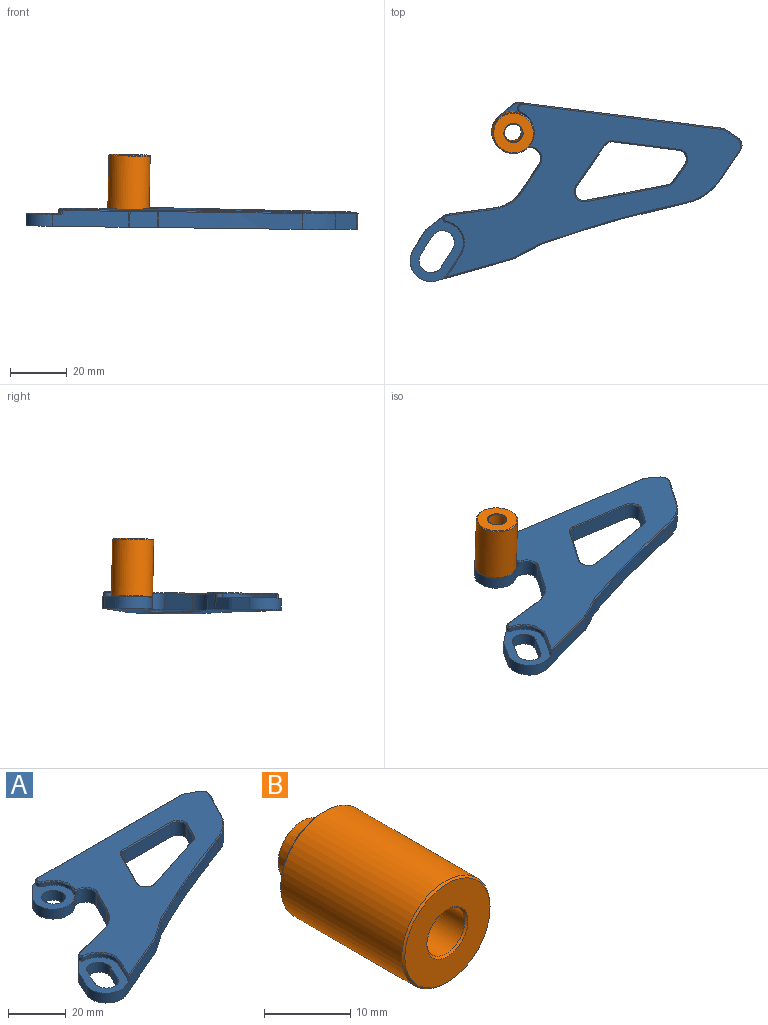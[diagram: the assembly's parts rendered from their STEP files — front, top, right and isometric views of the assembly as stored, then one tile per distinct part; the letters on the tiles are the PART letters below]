
ASSEMBLY  parts=2 mates=1
PART A: 80 faces, bbox 110.9x66.7x6.3 mm
  f0: plane 17.76x14.5mm, normal (0,0,1), area 122.4mm2, adj f1,f2,f3,f13,f14,f15,f16,f17
  f1: cylinder r=1.82mm len=3.56mm, axis (0,0,-1), area 7.5mm2, adj f0,f2,f13,f60
  f2: cylinder r=7.24mm len=10.45mm, axis (0,0,-1), area 18.8mm2, adj f0,f1,f3,f61
  f3: cylinder r=0.76mm len=1.45mm, axis (0,0,-1), area 2.3mm2, adj f0,f2,f17,f62
  f4: cylinder r=7.33mm len=1.72mm, axis (0,0,-1), area 3mm2, adj f5,f69,f70,f71
  f5: plane 6.75x3.15mm, normal (-0.91,0.42,0), area 10.8mm2, adj f4,f6,f50,f71
  f6: cylinder r=7.33mm len=10.42mm, axis (0,0,-1), area 21mm2, adj f5,f7,f49,f71
  f7: cylinder r=1.2mm len=2.05mm, axis (0,0,-1), area 4mm2, adj f6,f21,f68,f71
  f8: cylinder r=19.05mm len=10.67mm, axis (0,0,1), area 81.1mm2, adj f9,f26,f54,f73
  f9: plane 11.36x5.79mm, normal (0.89,-0.45,0), area 71.3mm2, adj f8,f10,f55,f73
  f10: cylinder r=3.17mm len=5.59mm, axis (0,0,1), area 27.9mm2, adj f9,f11,f56,f73
  f11: plane 5.59x4.46mm, normal (0.45,0.89,0), area 28mm2, adj f10,f12,f57,f73
  f12: cylinder r=3.17mm len=5.59mm, axis (0,0,1), area 8.4mm2, adj f11,f13,f58,f73
  f13: plane 71.53x5.59mm, normal (0,1,0), area 398mm2, adj f0,f1,f12,f14,f59,f73
  f14: cylinder r=3.17mm len=4.14mm, axis (0,0,1), area 10.7mm2, adj f0,f13,f15,f73
  f15: plane 4.54x4.31mm, normal (-0.72,0.69,0), area 25.9mm2, adj f0,f14,f16,f73
  f16: cylinder r=7.24mm len=12.23mm, axis (0,0,-1), area 90.8mm2, adj f0,f15,f17,f73
  f17: cylinder r=3.92mm len=6.45mm, axis (0,0,1), area 56.4mm2, adj f0,f3,f16,f18,f63,f73
  f18: plane 10.44x5.59mm, normal (-0.89,0.46,0), area 65.5mm2, adj f17,f19,f64,f73
  f19: cylinder r=12.7mm len=8.04mm, axis (0,0,1), area 59.4mm2, adj f18,f20,f65,f73
  f20: plane 15.92x5.59mm, normal (-0.26,0.97,0), area 92mm2, adj f19,f21,f66,f73
  f21: cylinder r=3.17mm len=5.59mm, axis (0,0,1), area 9.3mm2, adj f7,f20,f22,f67,f73
  f22: plane 5.41x5.41mm, normal (-0.71,0.71,0), area 31.7mm2, adj f21,f23,f71,f73
  f23: cylinder r=3.17mm len=4.14mm, axis (0,0,1), area 4.6mm2, adj f22,f24,f71,f73
  f24: plane 6.71x4.14mm, normal (-0.91,0.42,0), area 30.7mm2, adj f23,f71,f72,f73
  f25: cylinder r=3.17mm len=5.59mm, axis (0,0,1), area 2.5mm2, adj f26,f40,f52,f73
  f26: cylinder r=406.4mm len=48.32mm, axis (0,0,-1), area 293.6mm2, adj f8,f25,f53,f73
  f27: cylinder r=3.17mm len=5.59mm, axis (0,0,-1), area 19.5mm2, adj f28,f34,f48,f73
  f28: plane 23.14x5.59mm, normal (0,-1,0), area 129.3mm2, adj f27,f29,f41,f73
  f29: cylinder r=3.17mm len=5.59mm, axis (0,0,-1), area 36.2mm2, adj f28,f30,f42,f73
  f30: plane 6.39x5.59mm, normal (-0.89,0.45,0), area 40.1mm2, adj f29,f31,f43,f73
  f31: cylinder r=3.17mm len=5.59mm, axis (0,0,-1), area 13.9mm2, adj f30,f32,f44,f73
  f32: plane 27.77x9.02mm, normal (-0.31,0.95,0), area 163.2mm2, adj f31,f33,f45,f73
  f33: cylinder r=3.17mm len=5.59mm, axis (0,0,-1), area 41.8mm2, adj f32,f34,f46,f73
  f34: plane 15.41x7.89mm, normal (0.89,-0.46,0), area 96.8mm2, adj f27,f33,f47,f73
  f35: cylinder r=4.09mm len=8.18mm, axis (0,0,1), area 106.4mm2, adj f0,f73
  f36: plane 6.75x4.14mm, normal (-0.91,0.42,0), area 30.8mm2, adj f37,f39,f71,f73
  f37: cylinder r=4.23mm len=8.06mm, axis (0,0,1), area 55mm2, adj f36,f38,f71,f73
  f38: plane 6.75x4.14mm, normal (0.91,-0.42,0), area 30.8mm2, adj f37,f39,f71,f73
  f39: cylinder r=4.23mm len=8.06mm, axis (0,0,1), area 55mm2, adj f36,f38,f71,f73
  f40: plane 8.85x6.16mm, normal (0.57,-0.82,0), area 60.2mm2, adj f25,f51,f73,f74
  f41: plane 23.14x0.38mm, normal (0,-0.71,0.71), area 12.5mm2, adj f28,f42,f48,f76
  f42: cone r=3.37mm half-angle=45deg, axis (0,0,1), area 3.7mm2, adj f29,f41,f43,f76
  f43: plane 6.56x3.59mm, normal (-0.63,0.32,0.71), area 3.9mm2, adj f30,f42,f44,f76
  f44: cone r=3.37mm half-angle=45deg, axis (0,0,1), area 1.4mm2, adj f31,f43,f45,f76
  f45: plane 27.89x9.39mm, normal (-0.22,0.67,0.71), area 15.7mm2, adj f32,f44,f46,f76
  f46: cone r=3.37mm half-angle=45deg, axis (0,0,1), area 4.3mm2, adj f33,f45,f47,f76
  f47: plane 15.59x8.23mm, normal (0.63,-0.32,0.71), area 9.3mm2, adj f34,f46,f48,f76
  f48: cone r=3.37mm half-angle=45deg, axis (0,0,1), area 2mm2, adj f27,f41,f47,f76
  f49: cone r=7.52mm half-angle=45deg, axis (0,0,1), area 8mm2, adj f6,f50,f68,f76
  f50: plane 6.91x3.49mm, normal (-0.64,0.3,0.71), area 4mm2, adj f5,f49,f69,f76
  f51: plane 9.07x6.47mm, normal (0.4,-0.58,0.71), area 5.8mm2, adj f40,f52,f75,f76
  f52: cone r=3.37mm half-angle=45deg, axis (0,0,1), area 0.3mm2, adj f25,f51,f53,f76
  f53: cone r=406.59mm half-angle=45deg, axis (0,0,1), area 28.3mm2, adj f26,f52,f54,f76
  f54: cone r=18.86mm half-angle=45deg, axis (0,0,-1), area 7.7mm2, adj f8,f53,f55,f76
  f55: plane 11.53x6.13mm, normal (0.63,-0.32,0.71), area 6.9mm2, adj f9,f54,f56,f76
  f56: cone r=2.98mm half-angle=45deg, axis (0,0,-1), area 2.5mm2, adj f10,f55,f57,f76
  f57: plane 4.63x2.61mm, normal (0.32,0.63,0.71), area 2.7mm2, adj f11,f56,f58,f76
  f58: cone r=2.98mm half-angle=45deg, axis (0,0,-1), area 0.8mm2, adj f12,f57,f59,f76
  f59: plane 70.36x0.38mm, normal (0,0.71,0.71), area 37.9mm2, adj f13,f58,f60,f76
  f60: cone r=1.63mm half-angle=45deg, axis (0,0,-1), area 2.5mm2, adj f1,f59,f61,f76
  f61: cone r=7.43mm half-angle=45deg, axis (0,0,1), area 7.2mm2, adj f2,f60,f62,f76
  f62: cone r=0.57mm half-angle=45deg, axis (0,0,-1), area 0.7mm2, adj f3,f61,f63,f76
  f63: cone r=4.11mm half-angle=45deg, axis (0,0,1), area 4.6mm2, adj f17,f62,f64,f76
  f64: plane 10.61x5.69mm, normal (-0.63,0.32,0.71), area 6.3mm2, adj f18,f63,f65,f76
  f65: cone r=12.89mm half-angle=45deg, axis (0,0,1), area 5.8mm2, adj f19,f64,f66,f76
  f66: plane 16.01x4.61mm, normal (-0.18,0.68,0.71), area 8.9mm2, adj f20,f65,f67,f76
  f67: cone r=2.98mm half-angle=45deg, axis (0,0,-1), area 0.8mm2, adj f21,f66,f68,f76
  f68: cone r=1.01mm half-angle=45deg, axis (0,0,-1), area 1.3mm2, adj f7,f49,f67,f76
  f69: cone r=7.52mm half-angle=45deg, axis (0,0,1), area 1.1mm2, adj f4,f50,f76,f77
  f70: cylinder r=0.38mm len=1.45mm, axis (0,0,-1), area 1.5mm2, adj f4,f71,f77,f78
  f71: plane 23.52x17.92mm, normal (0,0,1), area 161mm2, adj f4,f5,f6,f7,f22,f23,f24,f36
  f72: cylinder r=7.33mm len=10.43mm, axis (0,0,-1), area 73.2mm2, adj f24,f71,f73,f78
  f73: plane 110.58x66.36mm, normal (0,0,-1), area 2774.8mm2, adj f8,f9,f10,f11,f12,f13,f14,f15
  f74: cylinder r=3.17mm len=5.59mm, axis (0,0,1), area 3.6mm2, adj f40,f73,f75,f78
  f75: cone r=2.98mm half-angle=45deg, axis (0,0,-1), area 0.3mm2, adj f51,f74,f76,f79
  f76: plane 100.24x63.64mm, normal (0,0,1), area 2342.5mm2, adj f41,f42,f43,f44,f45,f46,f47,f48
  f77: cone r=0.38mm half-angle=45deg, axis (0,0,-1), area 0.3mm2, adj f69,f70,f79
  f78: plane 25.31x10.87mm, normal (0.39,-0.92,0), area 149.1mm2, adj f70,f71,f72,f73,f74,f79
  f79: plane 22.72x10.23mm, normal (0.28,-0.65,0.71), area 13mm2, adj f75,f76,f77,f78
PART B: 12 faces, bbox 14.5x23.9x14.5 mm
  f0: cone r=4.27mm half-angle=45deg, axis (0,-1,0), area 9.6mm2, adj f1,f2
  f1: plane 14.23x13.97mm, normal (0,1,0), area 92.6mm2, adj f0,f3
  f2: cylinder r=4.14mm len=8.28mm, axis (0,-1,0), area 44.9mm2, adj f0,f4
  f3: cone r=7.11mm half-angle=45deg, axis (0,-1,0), area 16.1mm2, adj f1,f5
  f4: cone r=4.04mm half-angle=7.6deg, axis (0,-1,0), area 39mm2, adj f2,f6
  f5: cylinder r=7.24mm len=19.84mm, axis (0,1,0), area 902.3mm2, adj f3,f7
  f6: plane 8.02x7.87mm, normal (0,1,0), area 14.2mm2, adj f4,f8
  f7: cone r=7.11mm half-angle=45deg, axis (0,1,0), area 16.1mm2, adj f5,f9
  f8: cone r=3.21mm half-angle=14.9deg, axis (0,1,0), area 15.9mm2, adj f6,f10
  f9: plane 14.23x13.97mm, normal (0,-1,0), area 117.7mm2, adj f7,f11
  f10: cylinder r=3.11mm len=22.83mm, axis (0,-1,0), area 446.4mm2, adj f8,f11
  f11: cone r=3.24mm half-angle=45deg, axis (0,-1,0), area 7.3mm2, adj f9,f10
PLACE A rot(axis=(0.15,0.16,-0.98),7.4deg) t=(1.73,-0.8,14.52)mm
PLACE B rot(axis=(-1,0.07,-0.05),89.1deg) t=(2.2,-1.32,38.99)mm
MATE cylindrical A.f2 <-> B.f0  axis (0.02,-0.02,1) through (1.73,-0.8,14.52)mm
